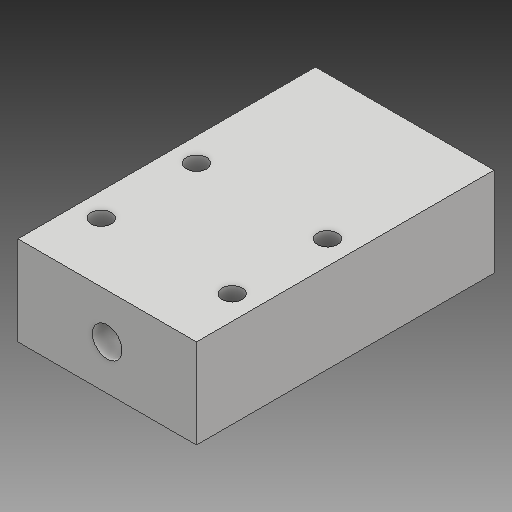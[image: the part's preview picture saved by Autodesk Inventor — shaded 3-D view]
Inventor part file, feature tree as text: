
AUTODESK INVENTOR PART (.ipt)
format: ipt  version: 2018 (Build 220112000, 112)  size: 100,864 bytes
history: native  units: mm
features: other x3, sketch x3
ambient origin geometry x8: Origin, YZ Plane, XZ Plane, XY Plane, X Axis, Y Axis, Z Axis, Center Point
bodies: Volumenkörper1 (feature_tree)
feature tree (6):
  other  "Gegenstück Rotorachse.ipt"
  other  "Volumenkörper1::Gegenstück Rotorachse.ipt"
  other  "Bezeichnung1"
  sketch  "Skizze1"  dims[d0=10.0mm]
  sketch  "Skizze2"
  sketch  "Skizze3"
